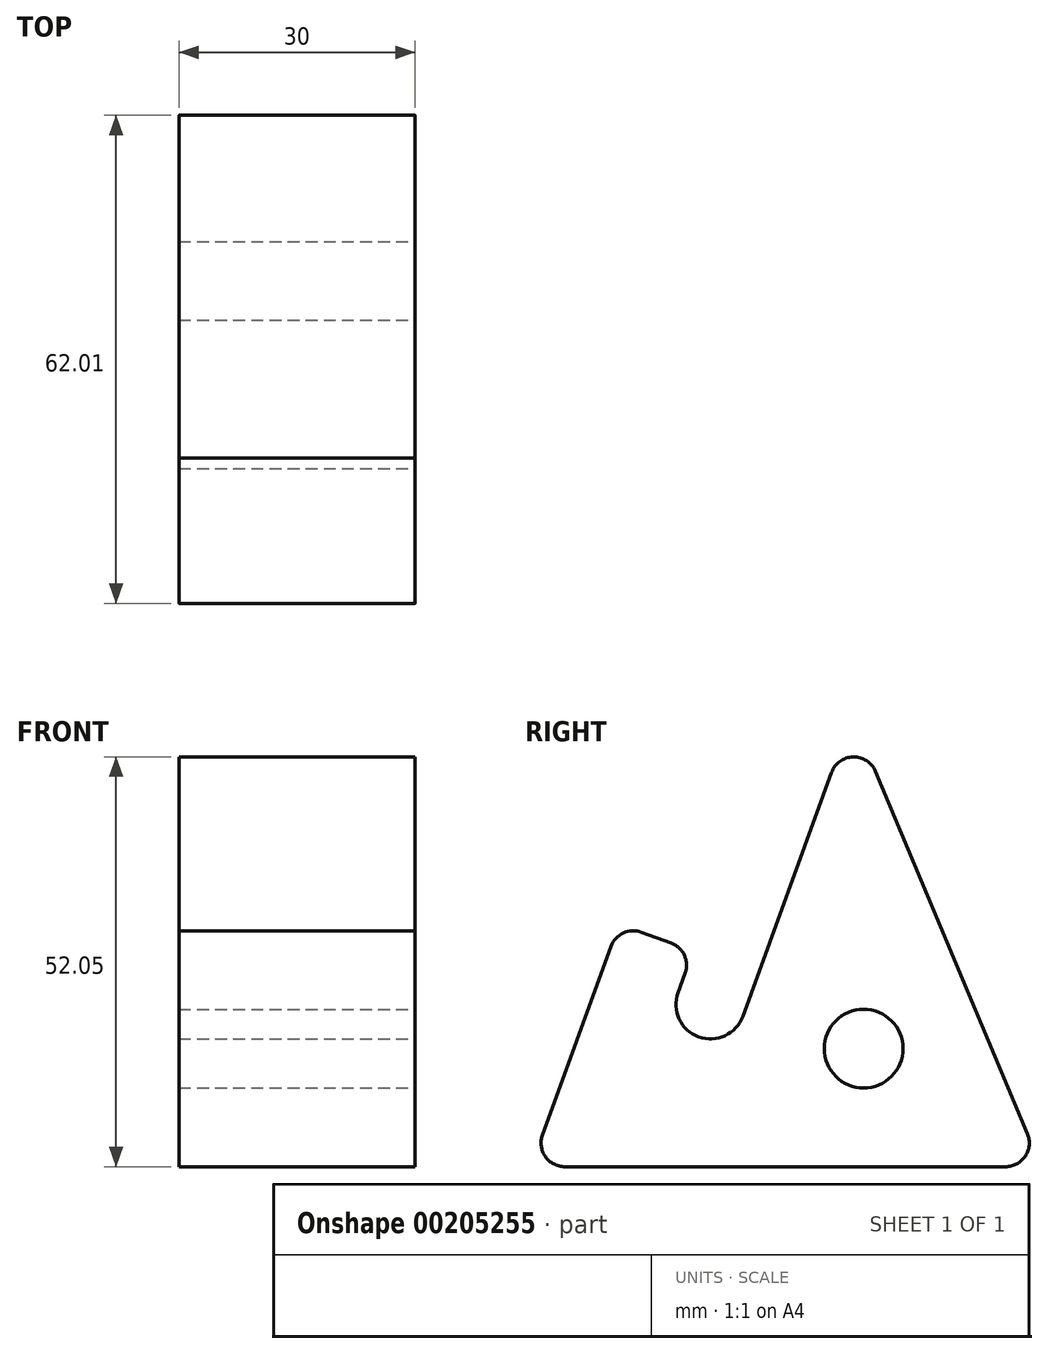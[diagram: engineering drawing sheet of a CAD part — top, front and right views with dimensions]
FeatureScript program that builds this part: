
annotation { "Feature Type Name" : "Feature", "Feature Type Description" : "" }
export const myFeature = defineFeature(function(context is Context, id is Id, definition is map)
    precondition{}
    {
        {
            assignVariable(context, id + "F0", {"name" : "grosortablet", "anyValue" : 8.75});
        }
        {
            assignVariable(context, id + "F1", {"name" : "anchosoporte", "anyValue" : 30});
        }
        {
            assignVariable(context, id + "F2", {"name" : "radiofillet", "anyValue" : 3});
        }
        {
            var Q0;
            Q0=qCreatedBy(makeId("Right.planeOp"),FACE);
            var sketch = newSketch(context, id + "F3", { "sketchPlane" : qUnion([Q0])});
            skLineSegment(sketch, "E0", {"start": v(-6, 0) * mm, "end": v(-70.8, 0) * mm});
            skLineSegment(sketch, "E1", {"start": v(-70.8, 0) * mm, "end": v(-59.6, 30.8) * mm});
            skLineSegment(sketch, "E2", {"start": v(-59.6, 30.8) * mm, "end": v(-50.2, 27.39) * mm});
            skLineSegment(sketch, "E3", {"start": v(-50.2, 27.39) * mm, "end": v(-53.62, 18) * mm});
            skLineSegment(sketch, "E4", {"start": v(-53.62, 18) * mm, "end": v(-45.4, 15) * mm});
            skLineSegment(sketch, "E5", {"start": v(-45.4, 15) * mm, "end": v(-30, 57.29) * mm});
            skLineSegment(sketch, "E6", {"start": v(-30, 57.29) * mm, "end": v(-6, 0) * mm});
            skSolve(sketch);
        }
        {
            var Q0;
            Q0=makeQuery(id+"F3.imprint","IMPRINT",FACE,{"disambiguationData":[TD([[makeQuery(id+"F3.imprint","IMPRINT",EDGE,{"derivedFrom":sQuery(id+"F3.wireOp",EDGE,"E0")}),-1.0]])]});
            extrude(context, id + "F4", {"entities" : qUnion([Q0]), "depth" : getVariable(context, 'anchosoporte') * mm});
        }
        {
            var Q0;
            Q0=makeQuery(id+"F4.opExtrude","SWEPT_EDGE",EDGE,{"disambiguationData":[OSD([sQuery(id+"F3.wireOp",EDGE,"E2"),sQuery(id+"F3.wireOp",EDGE,"E3")])]});
            var Q1;
            Q1=makeQuery(id+"F4.opExtrude","SWEPT_EDGE",EDGE,{"disambiguationData":[OSD([sQuery(id+"F3.wireOp",EDGE,"E5"),sQuery(id+"F3.wireOp",EDGE,"E6")])]});
            var Q2;
            Q2=makeQuery(id+"F4.opExtrude","SWEPT_EDGE",EDGE,{"disambiguationData":[OSD([sQuery(id+"F3.wireOp",EDGE,"E1"),sQuery(id+"F3.wireOp",EDGE,"E2")])]});
            var Q3;
            Q3=makeQuery(id+"F4.opExtrude","SWEPT_EDGE",EDGE,{"disambiguationData":[OSD([sQuery(id+"F3.wireOp",EDGE,"E0"),sQuery(id+"F3.wireOp",EDGE,"E1")])]});
            var Q4;
            Q4=makeQuery(id+"F4.opExtrude","SWEPT_EDGE",EDGE,{"disambiguationData":[OSD([sQuery(id+"F3.wireOp",EDGE,"E0"),sQuery(id+"F3.wireOp",EDGE,"E6")])]});
            fillet(context, id + "F5", {"entities" : qUnion([Q0, Q1, Q2, Q3, Q4]), "radius" : (getVariable(context, 'radiofillet')) * mm, "tangentPropagation" : true, "allowEdgeOverflow" : false});
        }
        {
            var Q0;
            Q0=makeQuery(id+"F4.opExtrude","CAP_FACE",FACE,{"disambiguationData":[OSD([sQuery(id+"F3.wireOp",EDGE,"E0"),sQuery(id+"F3.wireOp",EDGE,"E1"),sQuery(id+"F3.wireOp",EDGE,"E2"),sQuery(id+"F3.wireOp",EDGE,"E3"),sQuery(id+"F3.wireOp",EDGE,"E4"),sQuery(id+"F3.wireOp",EDGE,"E5"),sQuery(id+"F3.wireOp",EDGE,"E6")])],"isStart":false});
            var sketch = newSketch(context, id + "F6", { "sketchPlane" : qUnion([Q0])});
            skCircle(sketch, "E7", {"center": v(-28.55, 15) * mm, "radius": 5 * mm});
            skSolve(sketch);
        }
        {
            var Q0;
            Q0=makeQuery(id+"F6.imprint","IMPRINT",FACE,{"disambiguationData":[TD([[makeQuery(id+"F6.imprint","IMPRINT",EDGE,{"derivedFrom":sQuery(id+"F6.wireOp",EDGE,"E7")}),1.0]])]});
            extrude(context, id + "F7", {"entities" : qUnion([Q0]), "operationType" : NewBodyOperationType.REMOVE, "oppositeDirection" : true, "depth" : 33.1 * mm});
        }
        {
            var Q0;
            Q0=makeQuery(id+"F4.opExtrude","SWEPT_EDGE",EDGE,{"disambiguationData":[OSD([sQuery(id+"F3.wireOp",EDGE,"E3"),sQuery(id+"F3.wireOp",EDGE,"E4")])]});
            var Q1;
            Q1=makeQuery(id+"F4.opExtrude","SWEPT_EDGE",EDGE,{"disambiguationData":[OSD([sQuery(id+"F3.wireOp",EDGE,"E4"),sQuery(id+"F3.wireOp",EDGE,"E5")])]});
            fillet(context, id + "F8", {"entities" : qUnion([Q0, Q1]), "radius" : getVariable(context, 'grosortablet') / 2 * mm, "tangentPropagation" : true, "allowEdgeOverflow" : false});
        }
    });
